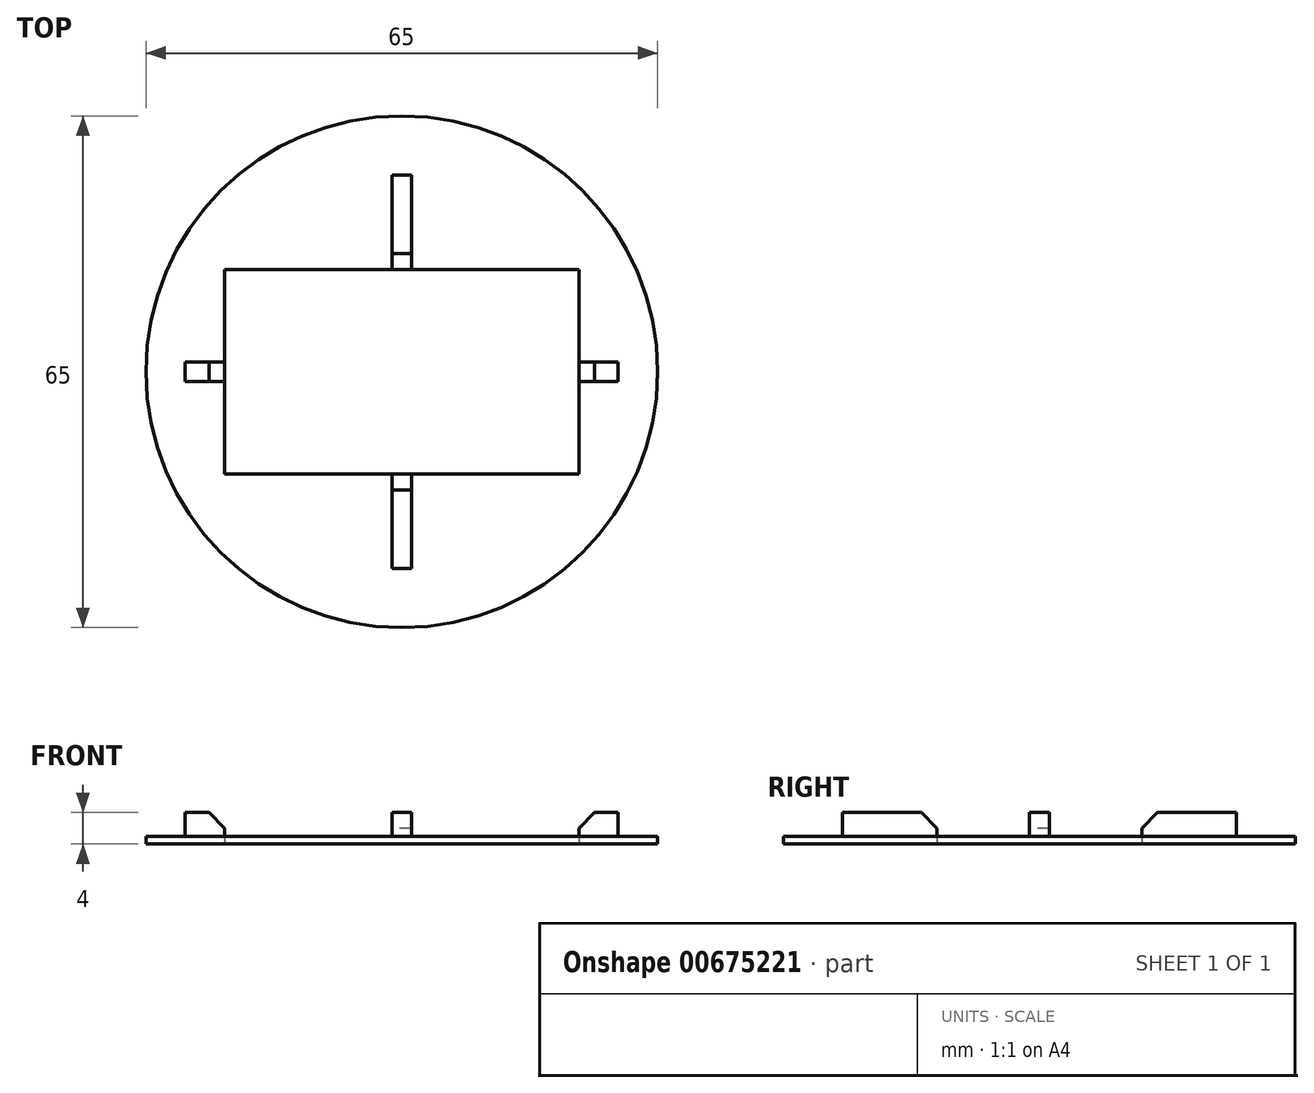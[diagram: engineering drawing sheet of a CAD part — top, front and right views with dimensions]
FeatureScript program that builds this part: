
annotation { "Feature Type Name" : "Feature", "Feature Type Description" : "" }
export const myFeature = defineFeature(function(context is Context, id is Id, definition is map)
    precondition{}
    {
        {
            var Q0;
            Q0=qCreatedBy(makeId("Top.planeOp"),FACE);
            var sketch = newSketch(context, id + "F0", { "sketchPlane" : qUnion([Q0])});
            skCircle(sketch, "E0", {"center": v(0, 0) * mm, "radius": 32.5 * mm});
            skLineSegment(sketch, "E1.bottom", {"start": v(-22.5, 13) * mm, "end": v(22.5, 13) * mm});
            skLineSegment(sketch, "E1.top", {"start": v(-22.5, -13) * mm, "end": v(22.5, -13) * mm});
            skLineSegment(sketch, "E1.left", {"start": v(-22.5, 13) * mm, "end": v(-22.5, -13) * mm});
            skLineSegment(sketch, "E1.right", {"start": v(22.5, 13) * mm, "end": v(22.5, -13) * mm});
            skSolve(sketch);
        }
        {
            var Q0;
            Q0 = qSketchRegion(id + "F0", true);
            extrude(context, id + "F1", {"entities" : qUnion([Q0]), "depth" : 1 * mm, "offsetDistance" : 25 * mm});
        }
        {
            var Q0;
            Q0=makeQuery(id+"F1.opExtrude","CAP_FACE",FACE,{"disambiguationData":[OSD([sQuery(id+"F0.wireOp",EDGE,"E0"),sQuery(id+"F0.wireOp",EDGE,"E1.bottom"),sQuery(id+"F0.wireOp",EDGE,"E1.top"),sQuery(id+"F0.wireOp",EDGE,"E1.left"),sQuery(id+"F0.wireOp",EDGE,"E1.right")])],"isStart":false});
            var sketch = newSketch(context, id + "F2", { "sketchPlane" : qUnion([Q0])});
            skLineSegment(sketch, "E2.bottom", {"start": v(-1.25, 25) * mm, "end": v(1.25, 25) * mm});
            skLineSegment(sketch, "E2.top", {"start": v(-1.25, 13) * mm, "end": v(1.25, 13) * mm});
            skLineSegment(sketch, "E2.left", {"start": v(-1.25, 25) * mm, "end": v(-1.25, 13) * mm});
            skLineSegment(sketch, "E2.right", {"start": v(1.25, 25) * mm, "end": v(1.25, 13) * mm});
            skLineSegment(sketch, "E3.bottom", {"start": v(-1.25, -13) * mm, "end": v(1.25, -13) * mm});
            skLineSegment(sketch, "E3.top", {"start": v(-1.25, -25) * mm, "end": v(1.25, -25) * mm});
            skLineSegment(sketch, "E3.left", {"start": v(-1.25, -13) * mm, "end": v(-1.25, -25) * mm});
            skLineSegment(sketch, "E3.right", {"start": v(1.25, -13) * mm, "end": v(1.25, -25) * mm});
            skLineSegment(sketch, "E4.bottom", {"start": v(-27.5, 1.25) * mm, "end": v(-22.5, 1.25) * mm});
            skLineSegment(sketch, "E4.top", {"start": v(-27.5, -1.25) * mm, "end": v(-22.5, -1.25) * mm});
            skLineSegment(sketch, "E4.left", {"start": v(-27.5, 1.25) * mm, "end": v(-27.5, -1.25) * mm});
            skLineSegment(sketch, "E4.right", {"start": v(-22.5, 1.25) * mm, "end": v(-22.5, -1.25) * mm});
            skLineSegment(sketch, "E5.bottom", {"start": v(22.5, 1.25) * mm, "end": v(27.5, 1.25) * mm});
            skLineSegment(sketch, "E5.top", {"start": v(22.5, -1.25) * mm, "end": v(27.5, -1.25) * mm});
            skLineSegment(sketch, "E5.left", {"start": v(22.5, 1.25) * mm, "end": v(22.5, -1.25) * mm});
            skLineSegment(sketch, "E5.right", {"start": v(27.5, 1.25) * mm, "end": v(27.5, -1.25) * mm});
            skSolve(sketch);
        }
        {
            var Q0;
            Q0 = qSketchRegion(id + "F2", true);
            extrude(context, id + "F3", {"entities" : qUnion([Q0]), "operationType" : NewBodyOperationType.ADD, "depth" : 3 * mm, "offsetDistance" : 25 * mm});
        }
        {
            var Q0;
            Q0=makeQuery(id+"F3.opExtrude","CAP_EDGE",EDGE,{"disambiguationData":[OSD([sQuery(id+"F2.wireOp",EDGE,"E4.right")])],"isStart":false});
            var Q1;
            Q1=makeQuery(id+"F3.opExtrude","CAP_EDGE",EDGE,{"disambiguationData":[OSD([sQuery(id+"F2.wireOp",EDGE,"E5.left")])],"isStart":false});
            var Q2;
            Q2=makeQuery(id+"F3.opExtrude","CAP_EDGE",EDGE,{"disambiguationData":[OSD([sQuery(id+"F2.wireOp",EDGE,"E2.top")])],"isStart":false});
            var Q3;
            Q3=makeQuery(id+"F3.opExtrude","CAP_EDGE",EDGE,{"disambiguationData":[OSD([sQuery(id+"F2.wireOp",EDGE,"E3.bottom")])],"isStart":false});
            chamfer(context, id + "F4", {"entities" : qUnion([Q0, Q1, Q2, Q3]), "width" : 2 * mm, "tangentPropagation" : true});
        }
    });
